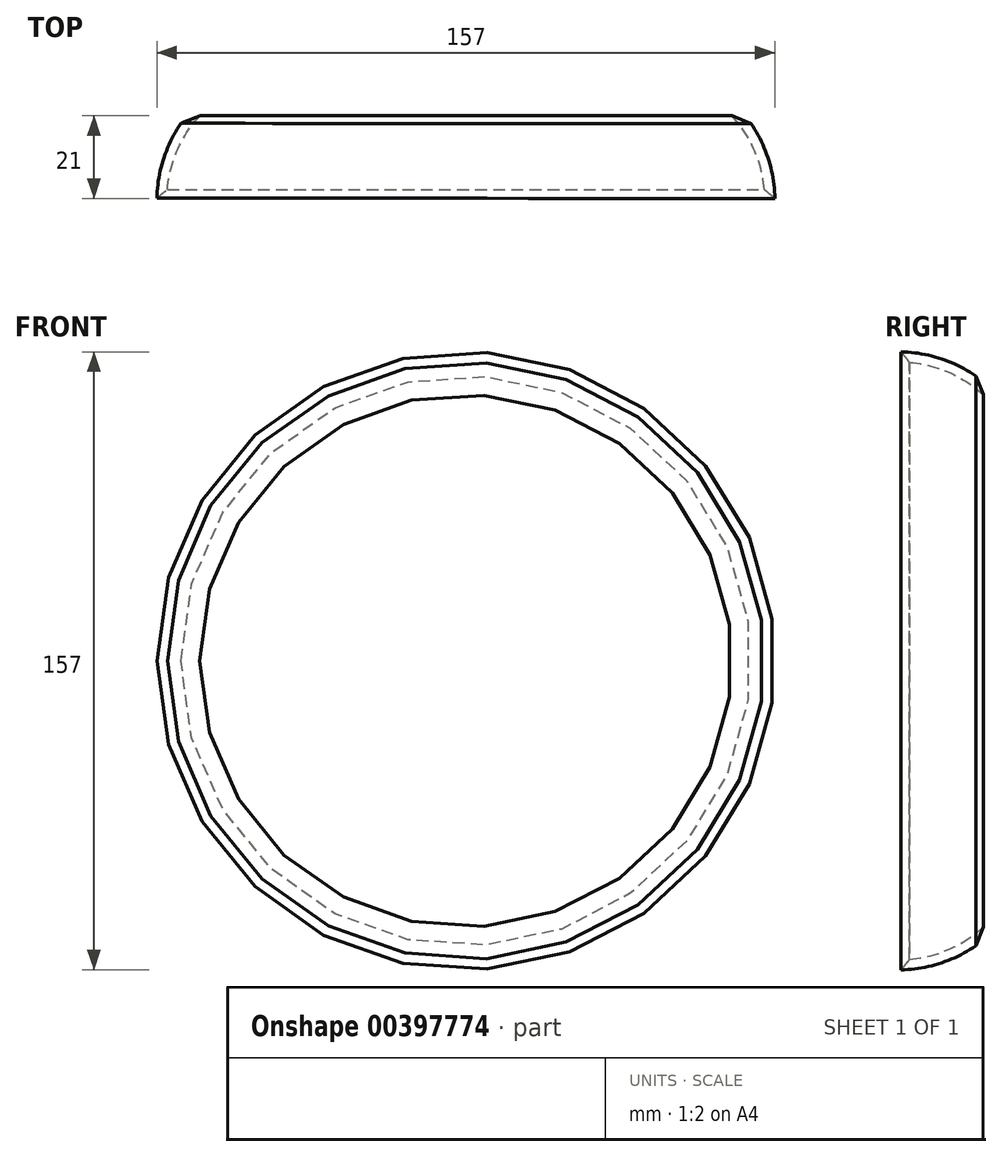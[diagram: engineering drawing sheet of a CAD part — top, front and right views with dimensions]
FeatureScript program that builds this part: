
annotation { "Feature Type Name" : "Feature", "Feature Type Description" : "" }
export const myFeature = defineFeature(function(context is Context, id is Id, definition is map)
    precondition{}
    {
        {
            var Q0;
            Q0=qCreatedBy(makeId("Top.planeOp"),FACE);
            var sketch = newSketch(context, id + "F0", { "sketchPlane" : qUnion([Q0])});
            skArc(sketch, "E0", {"start": v(0, 35.62) * mm, "mid": v(0.01, 36.72) * mm, "end": v(0, 37.82) * mm});
            skArc(sketch, "E1", {"start": v(-72.39, 33.24) * mm, "mid": v(-76.85, 24.17) * mm, "end": v(-78.51, 14.2) * mm});
            skArc(sketch, "E2", {"start": v(-78.51, 14.2) * mm, "mid": v(-88.81, -12.94) * mm, "end": v(-73.14, -37.4) * mm});
            skArc(sketch, "E3", {"start": v(-73.14, -37.4) * mm, "mid": v(-66.04, -50.33) * mm, "end": v(-52.74, -56.74) * mm});
            skArc(sketch, "E4.trimOffspring", {"start": v(-52.74, -56.74) * mm, "mid": v(-19.47, -64.93) * mm, "end": v(-0.01, -36.73) * mm});
            skLineSegment(sketch, "E5", {"start": v(0, 80.01) * mm, "end": v(-0.02, -68.12) * mm});
            skFitSpline(sketch, "E6", {"points": [v(-72.39, 33.24) * mm, v(-98.55, 24.24) * mm, v(-130.42, 19.24) * mm, v(-99.5, 38.61) * mm, v(-87.93, 51.11) * mm, v(-67.94, 61.73) * mm, v(-53.25, 50.49) * mm, v(-53.25, 69.86) * mm, v(-82.62, 70.17) * mm, v(-72.39, 76.1) * mm, v(-49.5, 72.98) * mm, v(-42, 9.25) * mm, v(-28.57, -3.87) * mm, v(-18.57, 26.43) * mm, v(-28.57, 57.67) * mm, v(0, 80.01) * mm], "startDerivative": vector(-313.71, -127.54) * mm, "endDerivative": vector(525.82, 263.39) * mm});
            skSolve(sketch);
        }
        {
            var Q0;
            {var subQ0=sQuery(id+"F0.wireOp",EDGE,"E0");Q0=makeQuery(id+"F0.imprint","IMPRINT",FACE,{"disambiguationData":[TD([[makeQuery(id+"F0.imprint","IMPRINT",EDGE,{"derivedFrom":subQ0}),1.0]])]});}
            var Q1;
            Q1=makeQuery(id+"F0.imprint","IMPRINT",FACE,{"disambiguationData":[TD([[makeQuery(id+"F0.imprint","IMPRINT",EDGE,{"derivedFrom":sQuery(id+"F0.wireOp",EDGE,"E1")}),1.0]])]});
            var Q2;
            Q2=sQuery(id+"F0.wireOp",EDGE,"E5");
            revolve(context, id + "F1", {"entities" : qUnion([Q0, Q1]), "axis" : qUnion([Q2]), "revolveType" : RevolveType.FULL});
        }
        {
            var Q0;
            Q0=makeQuery(id+"F1.opRevolve","SWEPT_FACE",FACE,{"disambiguationData":[OSD([sQuery(id+"F0.wireOp",EDGE,"E4.trimOffspring")])]});
            var Q1;
            Q1=makeQuery(id+"F1.opRevolve","SWEPT_FACE",FACE,{"disambiguationData":[OSD([sQuery(id+"F0.wireOp",EDGE,"E3")])]});
            var Q2;
            Q2=makeQuery(id+"F1.opRevolve","SWEPT_FACE",FACE,{"disambiguationData":[OSD([sQuery(id+"F0.wireOp",EDGE,"E2")])]});
            var Q3;
            Q3=makeQuery(id+"F1.opRevolve","SWEPT_FACE",FACE,{"disambiguationData":[OSD([sQuery(id+"F0.wireOp",EDGE,"E6")])]});
            shell(context, id + "F2", {"entities" : qUnion([Q0, Q1, Q2, Q3]), "thickness" : 2.54 * mm});
        }
    });
